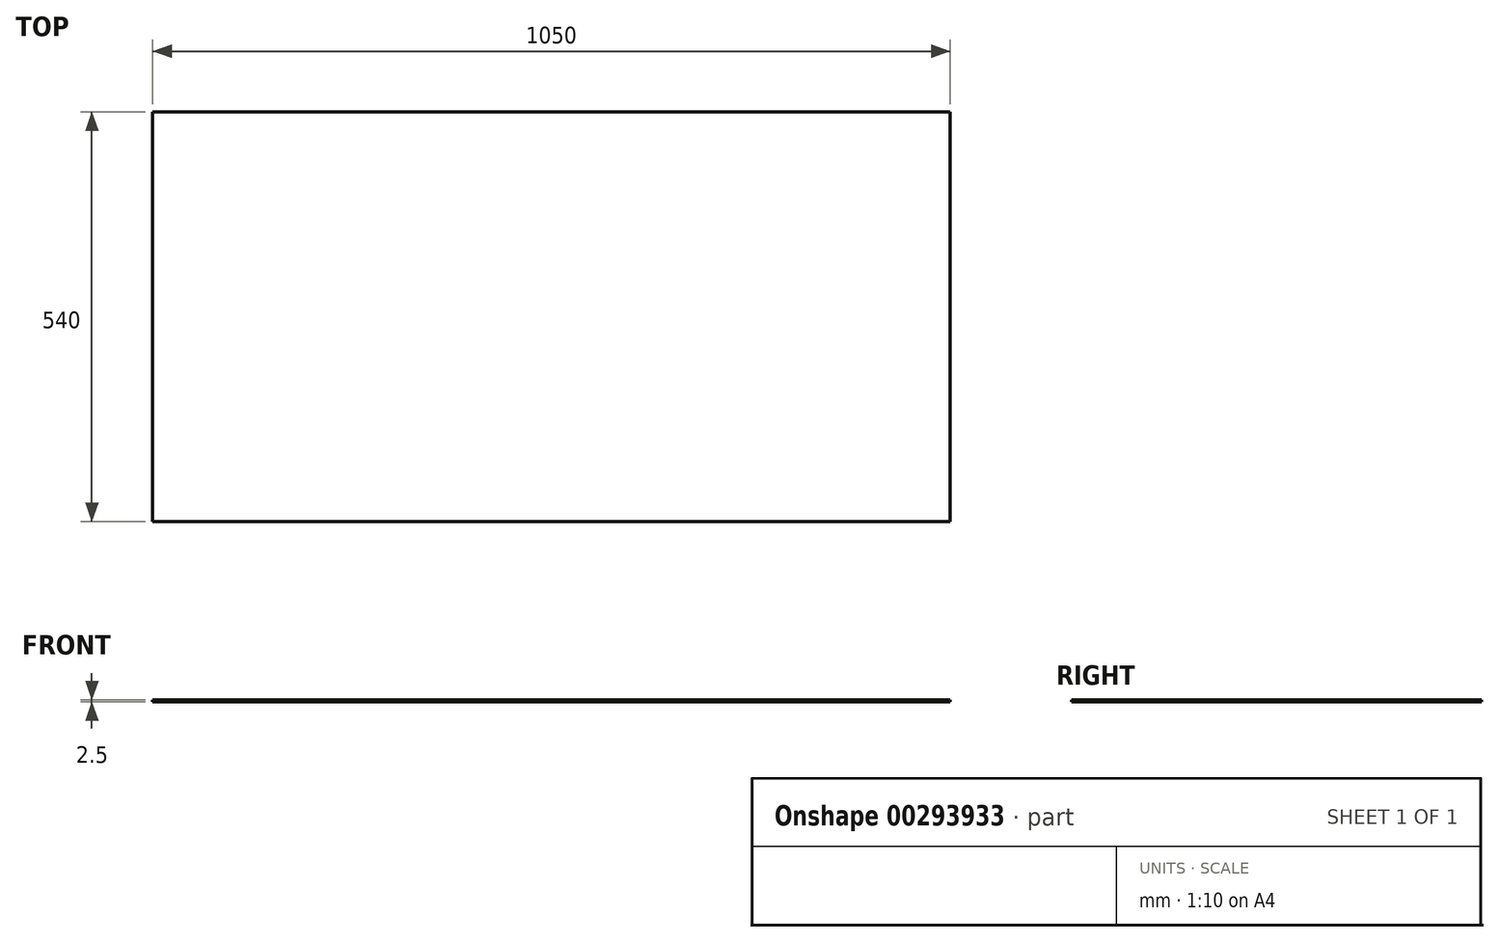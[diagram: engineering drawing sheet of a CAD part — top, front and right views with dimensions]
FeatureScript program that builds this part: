
annotation { "Feature Type Name" : "Feature", "Feature Type Description" : "" }
export const myFeature = defineFeature(function(context is Context, id is Id, definition is map)
    precondition{}
    {
        {
            var Q0;
            Q0=qCreatedBy(makeId("Top.planeOp"),FACE);
            var sketch = newSketch(context, id + "F0", { "sketchPlane" : qUnion([Q0])});
            skLineSegment(sketch, "E0.bottom", {"start": v(0, 0) * mm, "end": v(-1050, 0) * mm});
            skLineSegment(sketch, "E0.top", {"start": v(0, 540) * mm, "end": v(-1050, 540) * mm});
            skLineSegment(sketch, "E0.left", {"start": v(0, 0) * mm, "end": v(0, 540) * mm});
            skLineSegment(sketch, "E0.right", {"start": v(-1050, 0) * mm, "end": v(-1050, 540) * mm});
            skSolve(sketch);
        }
        {
            var Q0;
            Q0 = qSketchRegion(id + "F0", true);
            extrude(context, id + "F1", {"entities" : qUnion([Q0]), "depth" : 2.5 * mm});
        }
    });
